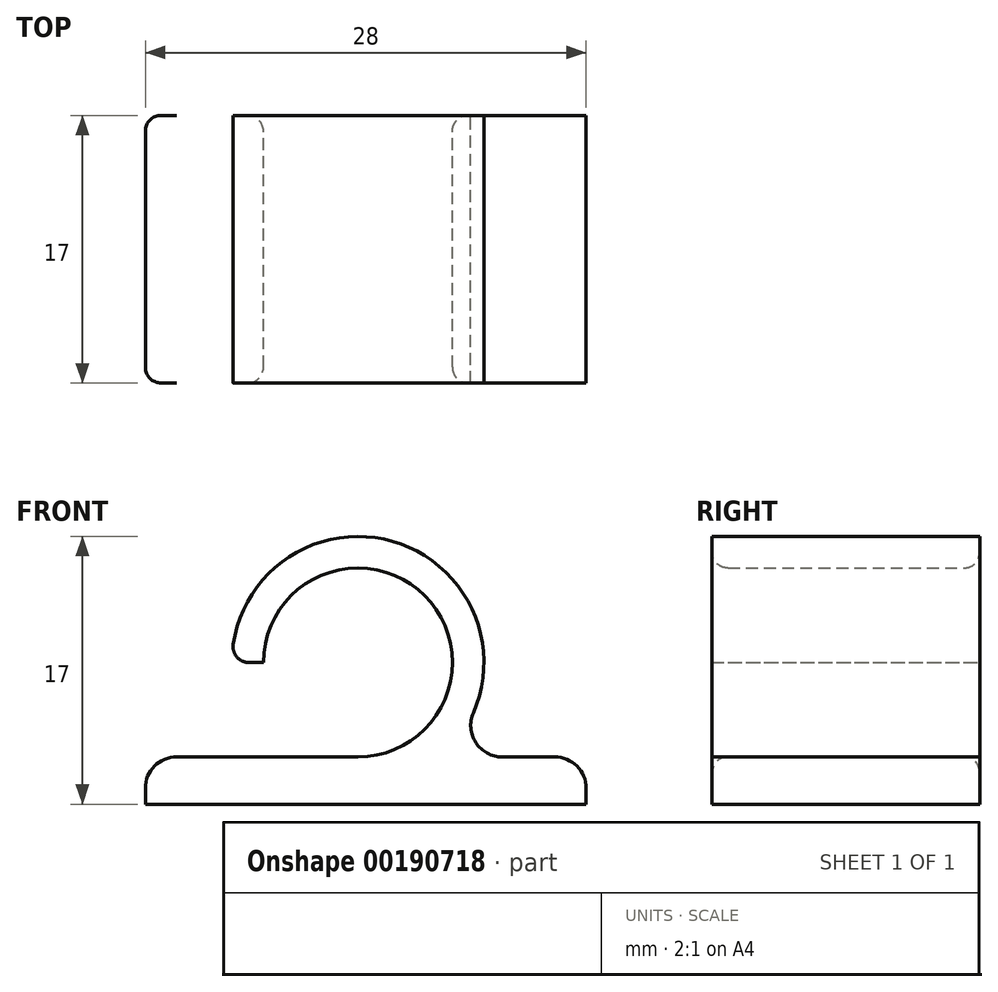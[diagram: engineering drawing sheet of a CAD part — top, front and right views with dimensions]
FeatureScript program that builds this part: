
annotation { "Feature Type Name" : "Feature", "Feature Type Description" : "" }
export const myFeature = defineFeature(function(context is Context, id is Id, definition is map)
    precondition{}
    {
        {
            var Q0;
            Q0=qCreatedBy(makeId("Front.planeOp"),FACE);
            var sketch = newSketch(context, id + "F0", { "sketchPlane" : qUnion([Q0])});
            skArc(sketch, "E0.0", {"start": v(13.5, 3) * mm, "mid": v(17.74, 13.24) * mm, "end": v(7.5, 9) * mm});
            skArc(sketch, "E1.0", {"start": v(20.83, 5.8) * mm, "mid": v(15.7, 16.7) * mm, "end": v(5.58, 10.14) * mm});
            skLineSegment(sketch, "E2.0", {"start": v(2, 3) * mm, "end": v(13.5, 3) * mm});
            skLineSegment(sketch, "E3.0", {"start": v(28, 1) * mm, "end": v(28, 0) * mm});
            skLineSegment(sketch, "E4.0", {"start": v(0, 0) * mm, "end": v(28, 0) * mm});
            skLineSegment(sketch, "E5.0", {"start": v(0, 1) * mm, "end": v(0, 0) * mm});
            skLineSegment(sketch, "E6.trimOffspring", {"start": v(22.67, 3) * mm, "end": v(26, 3) * mm});
            skLineSegment(sketch, "E7", {"start": v(6.57, 9) * mm, "end": v(7.5, 9) * mm});
            skArc(sketch, "E8.filletArc", {"start": v(20.83, 5.8) * mm, "mid": v(21, 3.9) * mm, "end": v(22.67, 3) * mm});
            skPoint(sketch, "E9.visualSharp", {"position": v(5.5, 9) * mm});
            skArc(sketch, "E9.filletArc", {"start": v(5.58, 10.14) * mm, "mid": v(5.82, 9.35) * mm, "end": v(6.57, 9) * mm});
            skPoint(sketch, "E10.visualSharp", {"position": v(0, 3) * mm});
            skArc(sketch, "E10.filletArc", {"start": v(2, 3) * mm, "mid": v(0.59, 2.41) * mm, "end": v(0, 1) * mm});
            skPoint(sketch, "E11.visualSharp", {"position": v(28, 3) * mm});
            skArc(sketch, "E11.filletArc", {"start": v(28, 1) * mm, "mid": v(27.41, 2.41) * mm, "end": v(26, 3) * mm});
            skSolve(sketch);
        }
        {
            var Q0;
            Q0 = qSketchRegion(id + "F0", true);
            extrude(context, id + "F1", {"entities" : qUnion([Q0]), "depth" : 17 * mm, "offsetDistance" : 25 * mm});
        }
        {
            var Q0;
            Q0=makeQuery(id+"F1.opExtrude","CAP_EDGE",EDGE,{"disambiguationData":[OSD([sQuery(id+"F0.wireOp",EDGE,"E2.0")])],"isStart":true});
            var Q1;
            Q1=makeQuery(id+"F1.opExtrude","CAP_EDGE",EDGE,{"disambiguationData":[OSD([sQuery(id+"F0.wireOp",EDGE,"E0.0")])],"isStart":false});
            fillet(context, id + "F2", {"entities" : qUnion([Q0, Q1]), "radius" : 1 * mm, "tangentPropagation" : true, "allowEdgeOverflow" : false});
        }
    });
